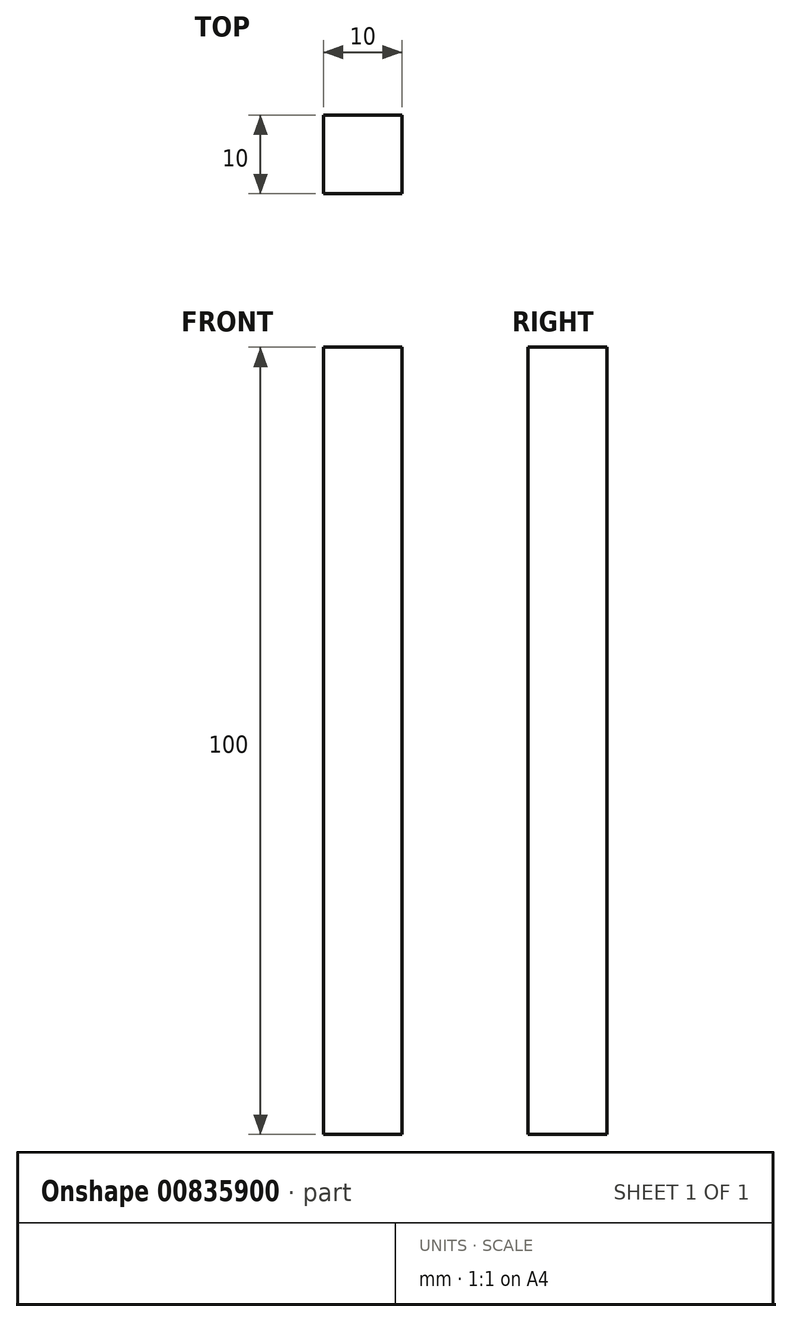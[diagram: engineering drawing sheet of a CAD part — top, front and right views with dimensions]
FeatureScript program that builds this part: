
annotation { "Feature Type Name" : "Feature", "Feature Type Description" : "" }
export const myFeature = defineFeature(function(context is Context, id is Id, definition is map)
    precondition{}
    {
        {
            var Q0;
            Q0=qCreatedBy(makeId("Top.planeOp"),FACE);
            var sketch = newSketch(context, id + "F0", { "sketchPlane" : qUnion([Q0])});
            skLineSegment(sketch, "E0.bottom", {"start": v(5, -5) * mm, "end": v(-5, -5) * mm});
            skLineSegment(sketch, "E0.top", {"start": v(5, 5) * mm, "end": v(-5, 5) * mm});
            skLineSegment(sketch, "E0.left", {"start": v(5, -5) * mm, "end": v(5, 5) * mm});
            skLineSegment(sketch, "E0.right", {"start": v(-5, -5) * mm, "end": v(-5, 5) * mm});
            skPoint(sketch, "E0.middle", {"position": v(0, 0) * mm});
            skSolve(sketch);
        }
        {
            var Q0;
            Q0=qSketchRegion(id+"F0",true);
            extrude(context, id + "F1", {"entities" : qUnion([Q0]), "depth" : 100 * mm, "offsetDistance" : 25 * mm});
        }
    });
